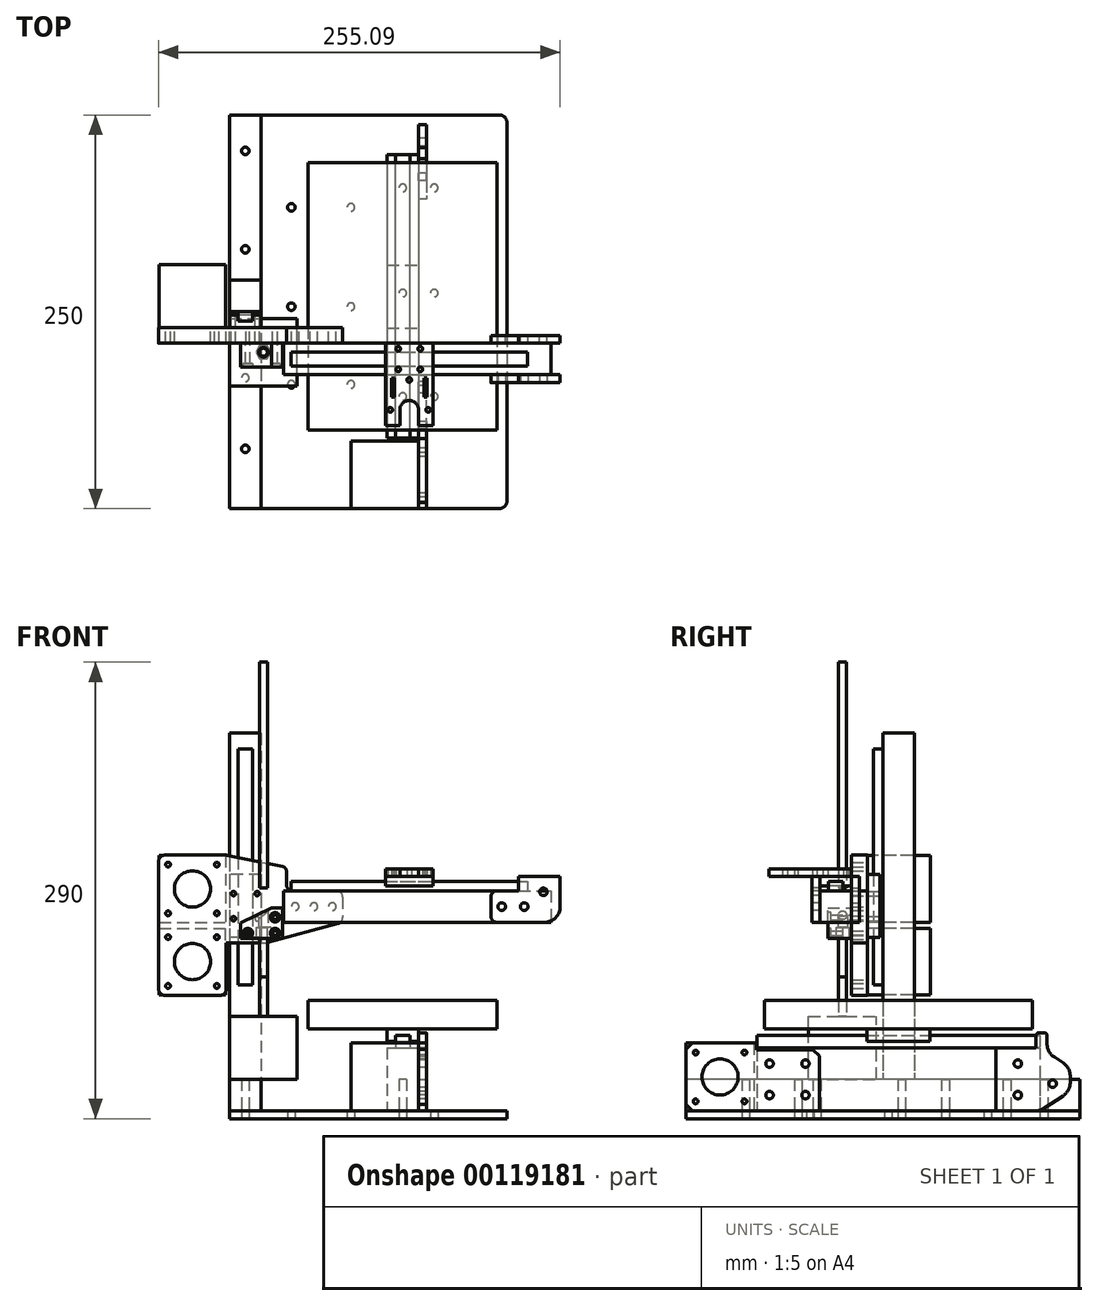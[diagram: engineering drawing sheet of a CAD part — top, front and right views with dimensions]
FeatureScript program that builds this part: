
annotation { "Feature Type Name" : "Feature", "Feature Type Description" : "" }
export const myFeature = defineFeature(function(context is Context, id is Id, definition is map)
    precondition{}
    {
        {
            var Q0;
            Q0=qCreatedBy(makeId("Top.planeOp"),FACE);
            var sketch = newSketch(context, id + "F0", { "sketchPlane" : qUnion([Q0])});
            skLineSegment(sketch, "E0.bottom", {"start": v(53.02, 129.2) * mm, "end": v(253.02, 129.2) * mm});
            skLineSegment(sketch, "E0.top", {"start": v(53.02, -120.8) * mm, "end": v(253.02, -120.8) * mm});
            skLineSegment(sketch, "E0.left", {"start": v(53.02, 129.2) * mm, "end": v(53.02, -120.8) * mm});
            skLineSegment(sketch, "E0.right", {"start": v(253.02, 129.2) * mm, "end": v(253.02, -120.8) * mm});
            skSolve(sketch);
        }
        {
            var Q0;
            Q0 = qSketchRegion(id + "F0", true);
            extrude(context, id + "F1", {"entities" : qUnion([Q0]), "depth" : 5 * mm});
        }
        {
            var Q0;
            Q0=makeQuery(id+"F1.opExtrude","CAP_FACE",FACE,{"disambiguationData":[OSD([sQuery(id+"F0.wireOp",EDGE,"E0.bottom"),sQuery(id+"F0.wireOp",EDGE,"E0.top"),sQuery(id+"F0.wireOp",EDGE,"E0.left"),sQuery(id+"F0.wireOp",EDGE,"E0.right")])],"isStart":false});
            var sketch = newSketch(context, id + "F2", { "sketchPlane" : qUnion([Q0])});
            skLineSegment(sketch, "E1.bottom", {"start": v(53.02, 129.2) * mm, "end": v(73.02, 129.2) * mm});
            skLineSegment(sketch, "E1.top", {"start": v(53.02, -120.8) * mm, "end": v(73.02, -120.8) * mm});
            skLineSegment(sketch, "E1.left", {"start": v(53.02, 129.2) * mm, "end": v(53.02, -120.8) * mm});
            skLineSegment(sketch, "E1.right", {"start": v(73.02, 129.2) * mm, "end": v(73.02, -120.8) * mm});
            skLineSegment(sketch, "E2.bottom", {"start": v(130.02, -120.8) * mm, "end": v(173.02, -120.8) * mm});
            skLineSegment(sketch, "E2.top", {"start": v(130.02, -77.8) * mm, "end": v(173.02, -77.8) * mm});
            skLineSegment(sketch, "E2.left", {"start": v(130.02, -120.8) * mm, "end": v(130.02, -77.8) * mm});
            skLineSegment(sketch, "E2.right", {"start": v(173.02, -120.8) * mm, "end": v(173.02, -77.8) * mm});
            skPoint(sketch, "E3.firstSnap0", {"position": v(153.02, 129.2) * mm});
            skLineSegment(sketch, "E3.bottom", {"start": v(153.02, 104) * mm, "end": v(173.02, 104) * mm});
            skLineSegment(sketch, "E3.top", {"start": v(153.02, -76) * mm, "end": v(173.02, -76) * mm});
            skLineSegment(sketch, "E3.left", {"start": v(153.02, 104) * mm, "end": v(153.02, -76) * mm});
            skLineSegment(sketch, "E3.right", {"start": v(173.02, 104) * mm, "end": v(173.02, -76) * mm});
            skSolve(sketch);
        }
        {
            var Q0;
            Q0=makeQuery(id+"F2.imprint","IMPRINT",FACE,{"disambiguationData":[TD([[makeQuery(id+"F2.imprint","IMPRINT",EDGE,{"derivedFrom":sQuery(id+"F2.wireOp",EDGE,"E1.bottom")}),-1.0]])]});
            var Q1;
            Q1=makeQuery(id+"F2.imprint","IMPRINT",FACE,{"disambiguationData":[TD([[makeQuery(id+"F2.imprint","IMPRINT",EDGE,{"derivedFrom":sQuery(id+"F2.wireOp",EDGE,"E3.bottom")}),-1.0]])]});
            extrude(context, id + "F3", {"entities" : qUnion([Q0, Q1]), "depth" : 40 * mm});
        }
        {
            var Q0;
            Q0=makeQuery(id+"F2.imprint","IMPRINT",FACE,{"disambiguationData":[TD([[makeQuery(id+"F2.imprint","IMPRINT",EDGE,{"derivedFrom":sQuery(id+"F2.wireOp",EDGE,"E2.bottom")}),1.0]])]});
            extrude(context, id + "F4", {"entities" : qUnion([Q0]), "depth" : 43 * mm});
        }
        {
            var Q0;
            Q0=makeQuery(id+"F3.opExtrude","CAP_FACE",FACE,{"disambiguationData":[OSD([sQuery(id+"F2.wireOp",EDGE,"E3.bottom"),sQuery(id+"F2.wireOp",EDGE,"E3.top"),sQuery(id+"F2.wireOp",EDGE,"E3.left"),sQuery(id+"F2.wireOp",EDGE,"E3.right")])],"isStart":false});
            var sketch = newSketch(context, id + "F5", { "sketchPlane" : qUnion([Q0])});
            skLineSegment(sketch, "E4.bottom", {"start": v(158.52, -76) * mm, "end": v(167.52, -76) * mm});
            skLineSegment(sketch, "E4.top", {"start": v(158.52, 104) * mm, "end": v(167.52, 104) * mm});
            skLineSegment(sketch, "E4.left", {"start": v(158.52, -76) * mm, "end": v(158.52, 104) * mm});
            skLineSegment(sketch, "E4.right", {"start": v(167.52, -76) * mm, "end": v(167.52, 104) * mm});
            skPoint(sketch, "E4.middle", {"position": v(163.02, 14) * mm});
            skPoint(sketch, "E4.middle.positionSnap0", {"position": v(163.02, -76) * mm});
            skPoint(sketch, "E4.middle.positionSnap1", {"position": v(153.02, 14) * mm});
            skPoint(sketch, "E4.centerSnap0", {"position": v(163.02, -76) * mm});
            skPoint(sketch, "E4.centerSnap1", {"position": v(153.02, 14) * mm});
            skSolve(sketch);
        }
        {
            var Q0;
            Q0 = qSketchRegion(id + "F5", true);
            extrude(context, id + "F6", {"entities" : qUnion([Q0]), "depth" : 8 * mm});
        }
        {
            var Q0;
            Q0=makeQuery(id+"F4.opExtrude","SWEPT_FACE",FACE,{"disambiguationData":[OSD([sQuery(id+"F2.wireOp",EDGE,"E2.right")])]});
            var sketch = newSketch(context, id + "F7", { "sketchPlane" : qUnion([Q0])});
            skCircle(sketch, "E5", {"center": v(-99.3, 26.5) * mm, "radius": 11.5 * mm});
            skPoint(sketch, "E5.centerSnap0", {"position": v(-120.8, 26.5) * mm});
            skPoint(sketch, "E5.centerSnap1", {"position": v(-99.3, 48) * mm});
            skLineSegment(sketch, "E6", {"start": v(-99.3, 26.5) * mm, "end": v(-77.8, 48) * mm, "construction": true});
            skLineSegment(sketch, "E7", {"start": v(-99.3, 48) * mm, "end": v(-99.3, 5) * mm, "construction": true});
            skLineSegment(sketch, "E8", {"start": v(-120.8, 26.5) * mm, "end": v(-77.8, 26.5) * mm, "construction": true});
            skCircle(sketch, "E9", {"center": v(-83.8, 42) * mm, "radius": 1.5 * mm});
            skCircle(sketch, "E10.MirrorC", {"center": v(-114.8, 42) * mm, "radius": 1.5 * mm});
            skCircle(sketch, "E11.MirrorC", {"center": v(-114.8, 11) * mm, "radius": 1.5 * mm});
            skCircle(sketch, "E12.MirrorC", {"center": v(-83.8, 11) * mm, "radius": 1.5 * mm});
            skLineSegment(sketch, "E13.bottom", {"start": v(-120.8, 5) * mm, "end": v(-76.27, 5) * mm});
            skLineSegment(sketch, "E13.top", {"start": v(-120.8, 48) * mm, "end": v(-76.27, 48) * mm});
            skLineSegment(sketch, "E13.left", {"start": v(-120.8, 5) * mm, "end": v(-120.8, 48) * mm});
            skLineSegment(sketch, "E13.right", {"start": v(-76.27, 43.73) * mm, "end": v(-76.27, 48) * mm});
            skLineSegment(sketch, "E14.bottom", {"start": v(-76.27, 43.73) * mm, "end": v(-36.27, 43.73) * mm});
            skLineSegment(sketch, "E14.top", {"start": v(-76.27, 5) * mm, "end": v(-36.27, 5) * mm});
            skLineSegment(sketch, "E14.right", {"start": v(-36.27, 43.73) * mm, "end": v(-36.27, 5) * mm});
            skLineSegment(sketch, "E15.0", {"start": v(104, 45) * mm, "end": v(104, 25) * mm});
            skLineSegment(sketch, "E16", {"start": v(104, 25) * mm, "end": v(88.12, 25) * mm, "construction": true});
            skPoint(sketch, "E17.orphan", {"position": v(104, 5) * mm});
            skLineSegment(sketch, "E18", {"start": v(104, 35) * mm, "end": v(-72.06, 35) * mm, "construction": true});
            skCircle(sketch, "E19", {"center": v(-67.87, 35) * mm, "radius": 2.4 * mm});
            skCircle(sketch, "E20", {"center": v(-45.03, 35) * mm, "radius": 2.4 * mm});
            skCircle(sketch, "E21.MirrorC", {"center": v(-67.87, 15) * mm, "radius": 2.4 * mm});
            skCircle(sketch, "E22.MirrorC", {"center": v(-45.03, 15) * mm, "radius": 2.4 * mm});
            skSolve(sketch);
        }
        {
            var Q0;
            Q0 = qSketchRegion(id + "F7", true);
            extrude(context, id + "F8", {"entities" : qUnion([Q0]), "depth" : 5 * mm});
        }
        {
            var Q0;
            Q0=makeQuery(id+"F8.opExtrude","SWEPT_EDGE",EDGE,{"disambiguationData":[OSD([sQuery(id+"F7.wireOp",EDGE,"E13.top"),sQuery(id+"F7.wireOp",EDGE,"E13.left")])]});
            var Q1;
            Q1=makeQuery(id+"F8.opExtrude","SWEPT_EDGE",EDGE,{"disambiguationData":[OSD([sQuery(id+"F7.wireOp",EDGE,"E13.bottom"),sQuery(id+"F7.wireOp",EDGE,"E13.left")])]});
            var Q2;
            Q2=makeQuery(id+"F8.opExtrude","SWEPT_EDGE",EDGE,{"disambiguationData":[OSD([sQuery(id+"F7.wireOp",EDGE,"E14.bottom"),sQuery(id+"F7.wireOp",EDGE,"E14.right")])]});
            chamfer(context, id + "F9", {"entities" : qUnion([Q0, Q1, Q2]), "width" : 4 * mm, "tangentPropagation" : true});
        }
        {
            var Q0;
            Q0=makeQuery(id+"F3.opExtrude","SWEPT_FACE",FACE,{"disambiguationData":[OSD([sQuery(id+"F2.wireOp",EDGE,"E3.right")])]});
            var sketch = newSketch(context, id + "F10", { "sketchPlane" : qUnion([Q0])});
            skLineSegment(sketch, "E23.0", {"start": v(104, 45) * mm, "end": v(104, 25) * mm, "construction": true});
            skLineSegment(sketch, "E24", {"start": v(104, 25) * mm, "end": v(84.3, 25) * mm, "construction": true});
            skPoint(sketch, "E25.orphan", {"position": v(104, 5) * mm});
            skCircle(sketch, "E26", {"center": v(89.85, 35) * mm, "radius": 2.4 * mm});
            skPoint(sketch, "E26.centerSnap0", {"position": v(104, 35) * mm});
            skCircle(sketch, "E27.MirrorC", {"center": v(89.85, 15) * mm, "radius": 2.4 * mm});
            skLineSegment(sketch, "E28.bottom", {"start": v(75.87, 45) * mm, "end": v(101.38, 45) * mm});
            skLineSegment(sketch, "E28.top", {"start": v(75.87, 5) * mm, "end": v(104, 5) * mm});
            skLineSegment(sketch, "E28.left", {"start": v(75.87, 45) * mm, "end": v(75.87, 5) * mm});
            skLineSegment(sketch, "E28.right", {"start": v(123.14, 32.4) * mm, "end": v(123.14, 17.6) * mm});
            skLineSegment(sketch, "E29", {"start": v(-99.33, 32.4) * mm, "end": v(131.84, 32.4) * mm, "construction": true});
            skCircle(sketch, "E30", {"center": v(111.96, 22.22) * mm, "radius": 10.5 * mm, "construction": true});
            skCircle(sketch, "E31", {"center": v(111.96, 22.22) * mm, "radius": 2.4 * mm});
            skLineSegment(sketch, "E32", {"start": v(108.43, 42.08) * mm, "end": v(123.14, 32.4) * mm});
            skLineSegment(sketch, "E33.MirrorCS", {"start": v(104, 5) * mm, "end": v(123.14, 17.6) * mm});
            skPoint(sketch, "E34.orphan", {"position": v(123.14, 5) * mm});
            skLineSegment(sketch, "E35.top", {"start": v(101.38, 54.64) * mm, "end": v(108.43, 54.64) * mm});
            skLineSegment(sketch, "E35.left", {"start": v(101.38, 45) * mm, "end": v(101.38, 54.64) * mm});
            skLineSegment(sketch, "E35.right", {"start": v(108.43, 42.08) * mm, "end": v(108.43, 54.64) * mm});
            skSolve(sketch);
        }
        {
            var Q0;
            Q0 = qSketchRegion(id + "F10", true);
            extrude(context, id + "F11", {"entities" : qUnion([Q0]), "depth" : 5 * mm});
        }
        {
            var Q0;
            Q0=makeQuery(id+"F11.opExtrude","SWEPT_EDGE",EDGE,{"disambiguationData":[OSD([sQuery(id+"F10.wireOp",EDGE,"E32"),sQuery(id+"F10.wireOp",EDGE,"E35.right")])]});
            var Q1;
            Q1=makeQuery(id+"F11.opExtrude","SWEPT_EDGE",EDGE,{"disambiguationData":[OSD([sQuery(id+"F10.wireOp",EDGE,"E28.right"),sQuery(id+"F10.wireOp",EDGE,"E32")])]});
            var Q2;
            Q2=makeQuery(id+"F11.opExtrude","SWEPT_EDGE",EDGE,{"disambiguationData":[OSD([sQuery(id+"F10.wireOp",EDGE,"E28.right"),sQuery(id+"F10.wireOp",EDGE,"E33.MirrorCS")])]});
            var Q3;
            Q3=makeQuery(id+"F11.opExtrude","SWEPT_EDGE",EDGE,{"disambiguationData":[OSD([sQuery(id+"F2.wireOp",EDGE,"E3.bottom"),sQuery(id+"F2.wireOp",EDGE,"E3.right"),sQuery(id+"F10.wireOp",EDGE,"E28.top"),sQuery(id+"F10.wireOp",EDGE,"E33.MirrorCS")])]});
            fillet(context, id + "F12", {"entities" : qUnion([Q0, Q1, Q2, Q3]), "radius" : 10 * mm, "tangentPropagation" : true, "allowEdgeOverflow" : false});
        }
        {
            var Q0;
            Q0=makeQuery(id+"F11.opExtrude","SWEPT_EDGE",EDGE,{"disambiguationData":[OSD([sQuery(id+"F10.wireOp",EDGE,"E35.top"),sQuery(id+"F10.wireOp",EDGE,"E35.right")])]});
            var Q1;
            Q1=makeQuery(id+"F11.opExtrude","SWEPT_EDGE",EDGE,{"disambiguationData":[OSD([sQuery(id+"F10.wireOp",EDGE,"E35.top"),sQuery(id+"F10.wireOp",EDGE,"E35.left")])]});
            fillet(context, id + "F13", {"entities" : qUnion([Q0, Q1]), "radius" : 2 * mm, "tangentPropagation" : true, "allowEdgeOverflow" : false});
        }
        {
            var Q0;
            Q0=makeQuery(id+"F6.opExtrude","CAP_FACE",FACE,{"disambiguationData":[OSD([sQuery(id+"F5.wireOp",EDGE,"E4.bottom"),sQuery(id+"F5.wireOp",EDGE,"E4.top"),sQuery(id+"F5.wireOp",EDGE,"E4.left"),sQuery(id+"F5.wireOp",EDGE,"E4.right")])],"isStart":false});
            var sketch = newSketch(context, id + "F14", { "sketchPlane" : qUnion([Q0])});
            skLineSegment(sketch, "E36.0", {"start": v(153.02, 104) * mm, "end": v(153.02, -76) * mm, "construction": true});
            skLineSegment(sketch, "E37.bottom", {"start": v(153.02, 34) * mm, "end": v(173.02, 34) * mm});
            skLineSegment(sketch, "E37.top", {"start": v(153.02, -6) * mm, "end": v(173.02, -6) * mm});
            skLineSegment(sketch, "E37.left", {"start": v(153.02, 34) * mm, "end": v(153.02, -6) * mm});
            skLineSegment(sketch, "E37.right", {"start": v(173.02, 34) * mm, "end": v(173.02, -6) * mm});
            skPoint(sketch, "E37.middle", {"position": v(163.02, 14) * mm});
            skPoint(sketch, "E37.middle.positionSnap0", {"position": v(163.02, -76) * mm});
            skPoint(sketch, "E37.middle.positionSnap1", {"position": v(167.52, 14) * mm});
            skPoint(sketch, "E37.centerSnap0", {"position": v(163.02, -76) * mm});
            skPoint(sketch, "E37.centerSnap1", {"position": v(167.52, 14) * mm});
            skSolve(sketch);
        }
        {
            var Q0;
            Q0 = qSketchRegion(id + "F14", true);
            extrude(context, id + "F15", {"entities" : qUnion([Q0]), "endBound" : BoundingType.SYMMETRIC, "depth" : 8 * mm});
        }
        {
            var Q0;
            Q0=makeQuery(id+"F0.imprint","IMPRINT",FACE,{"disambiguationData":[TD([[makeQuery(id+"F0.imprint","IMPRINT",EDGE,{"derivedFrom":sQuery(id+"F0.wireOp",EDGE,"E0.bottom")}),-1.0]])]});
            var sketch = newSketch(context, id + "F16", { "sketchPlane" : qUnion([Q0])});
            skLineSegment(sketch, "E38.0", {"start": v(153.02, 104) * mm, "end": v(173.02, 104) * mm, "construction": true});
            skLineSegment(sketch, "E39.0", {"start": v(73.02, 129.2) * mm, "end": v(73.02, -120.8) * mm, "construction": true});
            skLineSegment(sketch, "E40", {"start": v(73.02, -120.8) * mm, "end": v(53.02, -120.8) * mm, "construction": true});
            skCircle(sketch, "E41", {"center": v(63.02, -82.87) * mm, "radius": 2.4 * mm});
            skPoint(sketch, "E41.centerSnap0", {"position": v(63.02, -120.8) * mm});
            skCircle(sketch, "E42", {"center": v(63.02, -37.77) * mm, "radius": 2.4 * mm});
            skCircle(sketch, "E43", {"center": v(63.02, 43.87) * mm, "radius": 2.4 * mm});
            skCircle(sketch, "E44", {"center": v(63.02, 106.4) * mm, "radius": 2.4 * mm});
            skCircle(sketch, "E45", {"center": v(163.02, 82.91) * mm, "radius": 2.4 * mm});
            skPoint(sketch, "E45.centerSnap0", {"position": v(163.02, 104) * mm});
            skCircle(sketch, "E46", {"center": v(163.02, 16.05) * mm, "radius": 2.4 * mm});
            skCircle(sketch, "E47", {"center": v(163.02, -49.65) * mm, "radius": 2.4 * mm});
            skCircle(sketch, "E48", {"center": v(92.26, 70.57) * mm, "radius": 2.4 * mm});
            skCircle(sketch, "E49", {"center": v(130.12, 70.57) * mm, "radius": 2.4 * mm});
            skCircle(sketch, "E50", {"center": v(92.26, 7.46) * mm, "radius": 2.4 * mm});
            skCircle(sketch, "E51", {"center": v(130.12, 7.46) * mm, "radius": 2.4 * mm});
            skCircle(sketch, "E52", {"center": v(92.26, -41.93) * mm, "radius": 2.4 * mm});
            skCircle(sketch, "E53", {"center": v(130.12, -41.93) * mm, "radius": 2.4 * mm});
            skLineSegment(sketch, "E54.bottom", {"start": v(223.02, -73.95) * mm, "end": v(103.02, -73.95) * mm, "construction": true});
            skLineSegment(sketch, "E54.top", {"start": v(223.02, 106.05) * mm, "end": v(103.02, 106.05) * mm, "construction": true});
            skLineSegment(sketch, "E54.left", {"start": v(223.02, -73.95) * mm, "end": v(223.02, 106.05) * mm, "construction": true});
            skLineSegment(sketch, "E54.right", {"start": v(103.02, -73.95) * mm, "end": v(103.02, 106.05) * mm, "construction": true});
            skLineSegment(sketch, "E55.bottom", {"start": v(229.27, -124.8) * mm, "end": v(278.84, -124.8) * mm});
            skLineSegment(sketch, "E55.top", {"start": v(229.27, 139.17) * mm, "end": v(278.84, 139.17) * mm});
            skLineSegment(sketch, "E55.left", {"start": v(229.27, -124.8) * mm, "end": v(229.27, 139.17) * mm});
            skLineSegment(sketch, "E55.right", {"start": v(278.84, -124.8) * mm, "end": v(278.84, 139.17) * mm});
            skCircle(sketch, "E56.MirrorC", {"center": v(183.02, -49.65) * mm, "radius": 2.4 * mm});
            skCircle(sketch, "E57.MirrorC", {"center": v(183.02, 16.05) * mm, "radius": 2.4 * mm});
            skCircle(sketch, "E58.MirrorC", {"center": v(183.02, 82.91) * mm, "radius": 2.4 * mm});
            skSolve(sketch);
        }
        {
            var Q0;
            Q0 = qSketchRegion(id + "F16", true);
            extrude(context, id + "F17", {"entities" : qUnion([Q0]), "operationType" : NewBodyOperationType.REMOVE, "depth" : 25 * mm});
        }
        {
            var Q0;
            Q0=makeQuery(id+"F17.boolean.opBoolean","INTERSECT",EDGE,{"derivedFrom":[makeQuery(id+"F1.opExtrude","SWEPT_FACE",FACE,{"disambiguationData":[OSD([sQuery(id+"F0.wireOp",EDGE,"E0.top")])]}),makeQuery(id+"F17.opExtrude","SWEPT_FACE",FACE,{"disambiguationData":[OSD([sQuery(id+"F16.wireOp",EDGE,"E55.left")])]})]});
            var Q1;
            Q1=makeQuery(id+"F17.boolean.opBoolean","INTERSECT",EDGE,{"derivedFrom":[makeQuery(id+"F1.opExtrude","SWEPT_FACE",FACE,{"disambiguationData":[OSD([sQuery(id+"F0.wireOp",EDGE,"E0.bottom")])]}),makeQuery(id+"F17.opExtrude","SWEPT_FACE",FACE,{"disambiguationData":[OSD([sQuery(id+"F16.wireOp",EDGE,"E55.left")])]})]});
            fillet(context, id + "F18", {"entities" : qUnion([Q0, Q1]), "radius" : 5 * mm, "tangentPropagation" : true, "allowEdgeOverflow" : false});
        }
        {
            var Q0;
            Q0=makeQuery(id+"F3.opExtrude","CAP_FACE",FACE,{"disambiguationData":[OSD([sQuery(id+"F2.wireOp",EDGE,"E1.bottom"),sQuery(id+"F2.wireOp",EDGE,"E1.top"),sQuery(id+"F2.wireOp",EDGE,"E1.left"),sQuery(id+"F2.wireOp",EDGE,"E1.right")])],"isStart":false});
            extrude(context, id + "F19", {"entities" : qUnion([Q0]), "operationType" : NewBodyOperationType.REMOVE, "oppositeDirection" : true, "depth" : 20 * mm});
        }
        {
            var Q0;
            Q0=makeQuery(id+"F19.boolean.opBoolean","COPY",FACE,{"derivedFrom":makeQuery(id+"F19.opExtrude","CAP_FACE",FACE,{"disambiguationData":[OSD([sQuery(id+"F2.wireOp",EDGE,"E1.bottom"),sQuery(id+"F2.wireOp",EDGE,"E1.top"),sQuery(id+"F2.wireOp",EDGE,"E1.left"),sQuery(id+"F2.wireOp",EDGE,"E1.right")])],"isStart":false})});
            var sketch = newSketch(context, id + "F20", { "sketchPlane" : qUnion([Q0])});
            skLineSegment(sketch, "E59.bottom", {"start": v(73.02, 24.2) * mm, "end": v(53.02, 24.2) * mm});
            skLineSegment(sketch, "E59.top", {"start": v(73.02, 4.2) * mm, "end": v(53.02, 4.2) * mm});
            skLineSegment(sketch, "E59.left", {"start": v(73.02, 24.2) * mm, "end": v(73.02, 4.2) * mm});
            skLineSegment(sketch, "E59.right", {"start": v(53.02, 24.2) * mm, "end": v(53.02, 4.2) * mm});
            skSolve(sketch);
        }
        {
            var Q0;
            Q0 = qSketchRegion(id + "F20", true);
            extrude(context, id + "F21", {"entities" : qUnion([Q0]), "depth" : 220 * mm});
        }
        {
            var Q0;
            Q0=makeQuery(id+"F21.opExtrude","SWEPT_FACE",FACE,{"disambiguationData":[OSD([sQuery(id+"F20.wireOp",EDGE,"E59.top")])]});
            var sketch = newSketch(context, id + "F22", { "sketchPlane" : qUnion([Q0])});
            skLineSegment(sketch, "E60.bottom", {"start": v(67.52, 234.96) * mm, "end": v(58.52, 234.96) * mm});
            skLineSegment(sketch, "E60.top", {"start": v(67.52, 35.04) * mm, "end": v(58.52, 35.04) * mm});
            skLineSegment(sketch, "E60.left", {"start": v(67.52, 234.96) * mm, "end": v(67.52, 35.04) * mm});
            skLineSegment(sketch, "E60.right", {"start": v(58.52, 234.96) * mm, "end": v(58.52, 35.04) * mm});
            skPoint(sketch, "E60.middle", {"position": v(63.02, 135) * mm});
            skPoint(sketch, "E60.middle.positionSnap0", {"position": v(63.02, 245) * mm});
            skPoint(sketch, "E60.middle.positionSnap1", {"position": v(53.02, 135) * mm});
            skPoint(sketch, "E60.centerSnap0", {"position": v(63.02, 245) * mm});
            skPoint(sketch, "E60.centerSnap1", {"position": v(53.02, 135) * mm});
            skSolve(sketch);
        }
        {
            var Q0;
            Q0 = qSketchRegion(id + "F22", true);
            extrude(context, id + "F23", {"entities" : qUnion([Q0]), "depth" : 6 * mm});
        }
        {
            var Q0;
            Q0=makeQuery(id+"F23.opExtrude","CAP_FACE",FACE,{"disambiguationData":[OSD([sQuery(id+"F22.wireOp",EDGE,"E60.bottom"),sQuery(id+"F22.wireOp",EDGE,"E60.top"),sQuery(id+"F22.wireOp",EDGE,"E60.left"),sQuery(id+"F22.wireOp",EDGE,"E60.right")])],"isStart":false});
            var sketch = newSketch(context, id + "F24", { "sketchPlane" : qUnion([Q0])});
            skLineSegment(sketch, "E61.bottom", {"start": v(73.02, 155) * mm, "end": v(53.02, 155) * mm});
            skLineSegment(sketch, "E61.top", {"start": v(73.02, 115) * mm, "end": v(53.02, 115) * mm});
            skLineSegment(sketch, "E61.left", {"start": v(73.02, 155) * mm, "end": v(73.02, 115) * mm});
            skLineSegment(sketch, "E61.right", {"start": v(53.02, 155) * mm, "end": v(53.02, 115) * mm});
            skPoint(sketch, "E61.middle", {"position": v(63.02, 135) * mm});
            skPoint(sketch, "E61.middle.positionSnap0", {"position": v(67.52, 135) * mm});
            skPoint(sketch, "E61.middle.positionSnap1", {"position": v(63.02, 234.96) * mm});
            skPoint(sketch, "E61.centerSnap0", {"position": v(67.52, 135) * mm});
            skPoint(sketch, "E61.centerSnap1", {"position": v(63.02, 234.96) * mm});
            skLineSegment(sketch, "E62.bottom", {"start": v(70.52, 143) * mm, "end": v(55.52, 143) * mm, "construction": true});
            skLineSegment(sketch, "E62.top", {"start": v(70.52, 127) * mm, "end": v(55.52, 127) * mm, "construction": true});
            skLineSegment(sketch, "E62.left", {"start": v(70.52, 143) * mm, "end": v(70.52, 127) * mm, "construction": true});
            skLineSegment(sketch, "E62.right", {"start": v(55.52, 143) * mm, "end": v(55.52, 127) * mm, "construction": true});
            skCircle(sketch, "E63", {"center": v(55.52, 143) * mm, "radius": 1.4 * mm});
            skCircle(sketch, "E64", {"center": v(70.52, 143) * mm, "radius": 1.4 * mm});
            skCircle(sketch, "E65", {"center": v(55.52, 127) * mm, "radius": 1.4 * mm});
            skCircle(sketch, "E66", {"center": v(70.52, 127) * mm, "radius": 1.4 * mm});
            skSolve(sketch);
        }
        {
            var Q0;
            Q0 = qSketchRegion(id + "F24", true);
            extrude(context, id + "F25", {"entities" : qUnion([Q0]), "endBound" : BoundingType.SYMMETRIC, "depth" : 8 * mm});
        }
        {
            var Q0;
            Q0=makeQuery(id+"F23.opExtrude","SWEPT_FACE",FACE,{"disambiguationData":[OSD([sQuery(id+"F22.wireOp",EDGE,"E60.top")])]});
            extrude(context, id + "F26", {"entities" : qUnion([Q0]), "operationType" : NewBodyOperationType.REMOVE, "oppositeDirection" : true, "depth" : 50 * mm});
        }
        {
            var Q0;
            Q0=makeQuery(id+"F25.opExtrude","CAP_FACE",FACE,{"disambiguationData":[OSD([sQuery(id+"F24.wireOp",EDGE,"E61.bottom"),sQuery(id+"F24.wireOp",EDGE,"E61.top"),sQuery(id+"F24.wireOp",EDGE,"E61.left"),sQuery(id+"F24.wireOp",EDGE,"E61.right"),sQuery(id+"F24.wireOp",EDGE,"E63"),sQuery(id+"F24.wireOp",EDGE,"E64"),sQuery(id+"F24.wireOp",EDGE,"E65"),sQuery(id+"F24.wireOp",EDGE,"E66")])],"isStart":false});
            var sketch = newSketch(context, id + "F27", { "sketchPlane" : qUnion([Q0])});
            skLineSegment(sketch, "E67.bottom", {"start": v(89.11, 144.7) * mm, "end": v(259.11, 144.7) * mm, "construction": true});
            skLineSegment(sketch, "E67.top", {"start": v(89.11, 124.7) * mm, "end": v(259.11, 124.7) * mm, "construction": true});
            skLineSegment(sketch, "E67.left", {"start": v(89.11, 144.7) * mm, "end": v(89.11, 124.7) * mm, "construction": true});
            skLineSegment(sketch, "E67.right", {"start": v(259.11, 144.7) * mm, "end": v(259.11, 124.7) * mm, "construction": true});
            skCircle(sketch, "E68.0", {"center": v(55.52, 143) * mm, "radius": 1.4 * mm});
            skCircle(sketch, "E69.0", {"center": v(70.52, 143) * mm, "radius": 1.4 * mm});
            skCircle(sketch, "E70.0", {"center": v(70.52, 127) * mm, "radius": 1.4 * mm});
            skCircle(sketch, "E71.0", {"center": v(55.52, 127) * mm, "radius": 1.4 * mm});
            skLineSegment(sketch, "E72.bottom", {"start": v(156.82, 144.7) * mm, "end": v(165.82, 144.7) * mm, "construction": true});
            skLineSegment(sketch, "E72.top", {"start": v(156.82, 153.7) * mm, "end": v(165.82, 153.7) * mm, "construction": true});
            skLineSegment(sketch, "E72.left", {"start": v(156.82, 144.7) * mm, "end": v(156.82, 153.7) * mm, "construction": true});
            skLineSegment(sketch, "E72.right", {"start": v(165.82, 144.7) * mm, "end": v(165.82, 153.7) * mm, "construction": true});
            skLineSegment(sketch, "E73", {"start": v(156.82, 153.7) * mm, "end": v(17.3, 153.7) * mm, "construction": true});
            skLineSegment(sketch, "E74.bottom", {"start": v(50.93, 124.4) * mm, "end": v(7.93, 124.4) * mm, "construction": true});
            skLineSegment(sketch, "E74.top", {"start": v(50.93, 167.4) * mm, "end": v(7.93, 167.4) * mm, "construction": true});
            skLineSegment(sketch, "E74.left", {"start": v(50.93, 124.4) * mm, "end": v(50.93, 167.4) * mm, "construction": true});
            skLineSegment(sketch, "E74.right", {"start": v(7.93, 124.4) * mm, "end": v(7.93, 167.4) * mm, "construction": true});
            skPoint(sketch, "E74.middle", {"position": v(29.43, 145.9) * mm});
            skCircle(sketch, "E75", {"center": v(29.43, 145.9) * mm, "radius": 6 * mm, "construction": true});
            skLineSegment(sketch, "E76", {"start": v(268.66, 134.7) * mm, "end": v(73.02, 134.7) * mm, "construction": true});
            skPoint(sketch, "E76.startSnap0", {"position": v(89.11, 134.7) * mm});
            skLineSegment(sketch, "E77", {"start": v(50.93, 122.85) * mm, "end": v(4.58, 122.85) * mm, "construction": true});
            skLineSegment(sketch, "E78", {"start": v(29.43, 145.9) * mm, "end": v(50.93, 167.4) * mm, "construction": true});
            skLineSegment(sketch, "E79", {"start": v(29.43, 167.4) * mm, "end": v(29.43, 124.4) * mm, "construction": true});
            skLineSegment(sketch, "E80", {"start": v(7.93, 145.9) * mm, "end": v(50.93, 145.9) * mm, "construction": true});
            skCircle(sketch, "E81", {"center": v(44.93, 161.4) * mm, "radius": 1.5 * mm});
            skCircle(sketch, "E82.MirrorC", {"center": v(13.93, 161.4) * mm, "radius": 1.5 * mm});
            skCircle(sketch, "E83.MirrorC", {"center": v(44.93, 130.4) * mm, "radius": 1.5 * mm});
            skCircle(sketch, "E84.MirrorC", {"center": v(13.93, 130.4) * mm, "radius": 1.5 * mm});
            skCircle(sketch, "E85", {"center": v(29.43, 145.9) * mm, "radius": 11.5 * mm});
            skCircle(sketch, "E86.MirrorC", {"center": v(13.93, 84.3) * mm, "radius": 1.5 * mm});
            skLineSegment(sketch, "E87.MirrorCS", {"start": v(50.93, 121.3) * mm, "end": v(7.93, 121.3) * mm, "construction": true});
            skLineSegment(sketch, "E88.MirrorCS", {"start": v(50.93, 78.3) * mm, "end": v(7.93, 78.3) * mm, "construction": true});
            skLineSegment(sketch, "E89.MirrorCS", {"start": v(50.93, 121.3) * mm, "end": v(50.93, 78.3) * mm, "construction": true});
            skLineSegment(sketch, "E90.MirrorCS", {"start": v(29.43, 78.3) * mm, "end": v(29.43, 121.3) * mm, "construction": true});
            skCircle(sketch, "E91.MirrorC", {"center": v(44.93, 115.3) * mm, "radius": 1.5 * mm});
            skCircle(sketch, "E92.MirrorC", {"center": v(29.43, 99.8) * mm, "radius": 11.5 * mm});
            skLineSegment(sketch, "E93.MirrorCS", {"start": v(7.93, 121.3) * mm, "end": v(7.93, 78.3) * mm, "construction": true});
            skLineSegment(sketch, "E94.MirrorCS", {"start": v(29.43, 99.8) * mm, "end": v(50.93, 78.3) * mm, "construction": true});
            skLineSegment(sketch, "E95.MirrorCS", {"start": v(7.93, 99.8) * mm, "end": v(50.93, 99.8) * mm, "construction": true});
            skCircle(sketch, "E96.MirrorC", {"center": v(44.93, 84.3) * mm, "radius": 1.5 * mm});
            skCircle(sketch, "E97.MirrorC", {"center": v(13.93, 115.3) * mm, "radius": 1.5 * mm});
            skCircle(sketch, "E98.MirrorC", {"center": v(29.43, 99.8) * mm, "radius": 6 * mm, "construction": true});
            skLineSegment(sketch, "E99.bottom", {"start": v(7.93, 167.4) * mm, "end": v(50.93, 167.4) * mm});
            skLineSegment(sketch, "E99.top", {"start": v(7.93, 78.3) * mm, "end": v(50.93, 78.3) * mm});
            skLineSegment(sketch, "E99.left", {"start": v(7.93, 167.4) * mm, "end": v(7.93, 78.3) * mm});
            skLineSegment(sketch, "E99.right", {"start": v(124.85, 144.7) * mm, "end": v(124.85, 124.7) * mm});
            skCircle(sketch, "E100", {"center": v(94.67, 134.7) * mm, "radius": 2.4 * mm});
            skCircle(sketch, "E101", {"center": v(106.62, 134.7) * mm, "radius": 2.4 * mm});
            skCircle(sketch, "E102", {"center": v(118.31, 134.7) * mm, "radius": 2.4 * mm});
            skLineSegment(sketch, "E103", {"start": v(50.93, 167.4) * mm, "end": v(73.7, 162.82) * mm});
            skLineSegment(sketch, "E104", {"start": v(89.11, 144.7) * mm, "end": v(124.85, 144.7) * mm});
            skLineSegment(sketch, "E105", {"start": v(50.93, 78.3) * mm, "end": v(50.93, 111.72) * mm});
            skLineSegment(sketch, "E106", {"start": v(50.93, 111.72) * mm, "end": v(76.34, 111.72) * mm});
            skLineSegment(sketch, "E107", {"start": v(76.34, 111.72) * mm, "end": v(124.85, 124.7) * mm});
            skPoint(sketch, "E108.orphan", {"position": v(124.85, 78.3) * mm});
            skLineSegment(sketch, "E109.bottom", {"start": v(241.65, 124.7) * mm, "end": v(275.72, 124.7) * mm});
            skLineSegment(sketch, "E109.top", {"start": v(259.11, 153.9) * mm, "end": v(285.72, 153.9) * mm});
            skLineSegment(sketch, "E109.left", {"start": v(241.65, 124.7) * mm, "end": v(241.65, 144.7) * mm});
            skLineSegment(sketch, "E109.right", {"start": v(285.72, 134.7) * mm, "end": v(285.72, 153.9) * mm});
            skCircle(sketch, "E110", {"center": v(248.57, 134.7) * mm, "radius": 2.4 * mm});
            skCircle(sketch, "E111", {"center": v(262.85, 134.7) * mm, "radius": 2.4 * mm});
            skLineSegment(sketch, "E112", {"start": v(241.65, 144.7) * mm, "end": v(259.11, 144.7) * mm});
            skLineSegment(sketch, "E113", {"start": v(259.11, 144.7) * mm, "end": v(259.11, 159.61) * mm});
            skLineSegment(sketch, "E114", {"start": v(165.82, 153.7) * mm, "end": v(241.65, 153.82) * mm, "construction": true});
            skCircle(sketch, "E115", {"center": v(275.06, 144.07) * mm, "radius": 8 * mm, "construction": true});
            skCircle(sketch, "E116", {"center": v(275.06, 144.07) * mm, "radius": 2.4 * mm});
            skPoint(sketch, "E117.visualSharp", {"position": v(285.72, 124.7) * mm});
            skArc(sketch, "E117.filletArc", {"start": v(275.72, 124.7) * mm, "mid": v(282.8, 127.64) * mm, "end": v(285.72, 134.7) * mm});
            skLineSegment(sketch, "E118.trimOffspring", {"start": v(285.72, 153.88) * mm, "end": v(291.96, 153.9) * mm, "construction": true});
            skLineSegment(sketch, "E119.trimOffspring", {"start": v(241.65, 153.82) * mm, "end": v(241.65, 153.9) * mm});
            skLineSegment(sketch, "E120.top", {"start": v(285.72, 153.9) * mm, "end": v(259.11, 153.9) * mm});
            skLineSegment(sketch, "E120.left", {"start": v(285.72, 150.28) * mm, "end": v(285.72, 153.9) * mm});
            skLineSegment(sketch, "E120.right", {"start": v(259.11, 153.9) * mm, "end": v(259.11, 159.61) * mm});
            skPoint(sketch, "E121", {"position": v(74.62, 113.7) * mm});
            skCircle(sketch, "E122", {"center": v(64.61, 117.89) * mm, "radius": 1.25 * mm});
            skCircle(sketch, "E123", {"center": v(81.96, 117.89) * mm, "radius": 1.5 * mm});
            skCircle(sketch, "E124", {"center": v(81.96, 127.9) * mm, "radius": 1.5 * mm});
            skLineSegment(sketch, "E125", {"start": v(73.7, 162.82) * mm, "end": v(89.11, 159.7) * mm});
            skLineSegment(sketch, "E126", {"start": v(89.11, 159.7) * mm, "end": v(89.11, 144.7) * mm});
            skPoint(sketch, "E127.orphan", {"position": v(74.27, 144.7) * mm});
            skSolve(sketch);
        }
        {
            var Q0;
            Q0 = qSketchRegion(id + "F27", true);
            extrude(context, id + "F28", {"entities" : qUnion([Q0]), "depth" : 10 * mm});
        }
        {
            var Q0;
            Q0=makeQuery(id+"F28.opExtrude","SWEPT_EDGE",EDGE,{"disambiguationData":[OSD([sQuery(id+"F27.wireOp",EDGE,"TEMbkpEK-8kXP-iDgy-SPFr-wUDxhQlcmG9e"),sQuery(id+"F27.wireOp",EDGE,"E104")])]});
            var Q1;
            Q1=makeQuery(id+"F28.opExtrude","SWEPT_EDGE",EDGE,{"disambiguationData":[OSD([sQuery(id+"F27.wireOp",EDGE,"E103"),sQuery(id+"F27.wireOp",EDGE,"TEMbkpEK-8kXP-iDgy-SPFr-wUDxhQlcmG9e")])]});
            var Q2;
            Q2=makeQuery(id+"F28.opExtrude","SWEPT_EDGE",EDGE,{"disambiguationData":[OSD([sQuery(id+"F27.wireOp",EDGE,"E99.bottom"),sQuery(id+"F27.wireOp",EDGE,"E103")])]});
            var Q3;
            Q3=makeQuery(id+"F28.opExtrude","SWEPT_EDGE",EDGE,{"disambiguationData":[OSD([sQuery(id+"F27.wireOp",EDGE,"E99.right"),sQuery(id+"F27.wireOp",EDGE,"E104")])]});
            var Q4;
            Q4=makeQuery(id+"F28.opExtrude","SWEPT_EDGE",EDGE,{"disambiguationData":[OSD([sQuery(id+"F27.wireOp",EDGE,"E99.right"),sQuery(id+"F27.wireOp",EDGE,"E107")])]});
            var Q5;
            Q5=makeQuery(id+"F28.opExtrude","SWEPT_EDGE",EDGE,{"disambiguationData":[OSD([sQuery(id+"F27.wireOp",EDGE,"E99.bottom"),sQuery(id+"F27.wireOp",EDGE,"E99.left")])]});
            var Q6;
            Q6=makeQuery(id+"F28.opExtrude","SWEPT_EDGE",EDGE,{"disambiguationData":[OSD([sQuery(id+"F27.wireOp",EDGE,"E99.top"),sQuery(id+"F27.wireOp",EDGE,"E99.left")])]});
            var Q7;
            Q7=makeQuery(id+"F28.opExtrude","SWEPT_EDGE",EDGE,{"disambiguationData":[OSD([sQuery(id+"F27.wireOp",EDGE,"E99.top"),sQuery(id+"F27.wireOp",EDGE,"E105")])]});
            var Q8;
            Q8=makeQuery(id+"F28.opExtrude","SWEPT_EDGE",EDGE,{"disambiguationData":[OSD([sQuery(id+"F27.wireOp",EDGE,"E106"),sQuery(id+"F27.wireOp",EDGE,"E107")])]});
            var Q9;
            Q9=makeQuery(id+"F28.opExtrude","SWEPT_EDGE",EDGE,{"disambiguationData":[OSD([sQuery(id+"F27.wireOp",EDGE,"E120.top"),sQuery(id+"F27.wireOp",EDGE,"E120.left")])]});
            var Q10;
            Q10=makeQuery(id+"F28.opExtrude","SWEPT_EDGE",EDGE,{"disambiguationData":[OSD([sQuery(id+"F27.wireOp",EDGE,"E120.top"),sQuery(id+"F27.wireOp",EDGE,"E120.right")])]});
            var Q11;
            Q11=makeQuery(id+"F28.opExtrude","SWEPT_EDGE",EDGE,{"disambiguationData":[OSD([sQuery(id+"F27.wireOp",EDGE,"E109.left"),sQuery(id+"F27.wireOp",EDGE,"E112")])]});
            var Q12;
            Q12=makeQuery(id+"F28.opExtrude","SWEPT_EDGE",EDGE,{"disambiguationData":[OSD([sQuery(id+"F27.wireOp",EDGE,"E109.bottom"),sQuery(id+"F27.wireOp",EDGE,"E109.left")])]});
            fillet(context, id + "F29", {"entities" : qUnion([Q0, Q1, Q2, Q3, Q4, Q5, Q6, Q7, Q8, Q9, Q10, Q11, Q12]), "radius" : 4 * mm, "tangentPropagation" : true, "allowEdgeOverflow" : false});
        }
        {
            var Q0;
            Q0=qCreatedBy(makeId("Front.planeOp"),FACE);
            var sketch = newSketch(context, id + "F30", { "sketchPlane" : qUnion([Q0])});
            skPoint(sketch, "E128.0", {"position": v(53.02, 25) * mm});
            skLineSegment(sketch, "E129.bottom", {"start": v(53.02, 25) * mm, "end": v(96.02, 25) * mm});
            skLineSegment(sketch, "E129.top", {"start": v(53.02, 65) * mm, "end": v(96.02, 65) * mm});
            skLineSegment(sketch, "E129.left", {"start": v(53.02, 25) * mm, "end": v(53.02, 65) * mm});
            skLineSegment(sketch, "E129.right", {"start": v(96.02, 25) * mm, "end": v(96.02, 65) * mm});
            skSolve(sketch);
        }
        {
            var Q0;
            Q0 = qSketchRegion(id + "F30", true);
            extrude(context, id + "F31", {"entities" : qUnion([Q0]), "depth" : 43 * mm});
        }
        {
            var Q0;
            Q0=makeQuery(id+"F31.opExtrude","SWEPT_FACE",FACE,{"disambiguationData":[OSD([sQuery(id+"F30.wireOp",EDGE,"E129.top")])]});
            var sketch = newSketch(context, id + "F32", { "sketchPlane" : qUnion([Q0])});
            skSolve(sketch);
        }
        {
            var Q0;
            {var subQ0=sQuery(id+"F30.wireOp",EDGE,"E129.top");Q0=makeQuery(id+"F32.imprint","IMPRINT",FACE,{"disambiguationData":[TD([[makeQuery(id+"F32.imprint","IMPRINT",EDGE,{"derivedFrom":makeQuery(id+"F31.opExtrude","CAP_EDGE",EDGE,{"disambiguationData":[OSD([subQ0])],"isStart":true})}),-1.0]])]});}
            var sketch = newSketch(context, id + "F33", { "sketchPlane" : qUnion([Q0])});
            skLineSegment(sketch, "E130.0", {"start": v(53.02, -43) * mm, "end": v(96.02, -43) * mm, "construction": true});
            skLineSegment(sketch, "E131.0", {"start": v(96.02, -43) * mm, "end": v(96.02, 0) * mm, "construction": true});
            skCircle(sketch, "E132", {"center": v(74.52, -21.5) * mm, "radius": 2.5 * mm});
            skPoint(sketch, "E132.centerSnap0", {"position": v(96.02, -21.5) * mm});
            skPoint(sketch, "E132.centerSnap1", {"position": v(74.52, -43) * mm});
            skSolve(sketch);
        }
        {
            var Q0;
            Q0 = qSketchRegion(id + "F33", true);
            extrude(context, id + "F34", {"entities" : qUnion([Q0]), "operationType" : NewBodyOperationType.ADD, "depth" : 25 * mm});
        }
        {
            var Q0;
            Q0=makeQuery(id+"F28.opExtrude","CAP_FACE",FACE,{"disambiguationData":[OSD([sQuery(id+"F27.wireOp",EDGE,"E68.0"),sQuery(id+"F27.wireOp",EDGE,"E69.0"),sQuery(id+"F27.wireOp",EDGE,"E70.0"),sQuery(id+"F27.wireOp",EDGE,"E71.0"),sQuery(id+"F27.wireOp",EDGE,"E81"),sQuery(id+"F27.wireOp",EDGE,"E82.MirrorC"),sQuery(id+"F27.wireOp",EDGE,"E83.MirrorC"),sQuery(id+"F27.wireOp",EDGE,"E84.MirrorC"),sQuery(id+"F27.wireOp",EDGE,"E85"),sQuery(id+"F27.wireOp",EDGE,"E86.MirrorC"),sQuery(id+"F27.wireOp",EDGE,"E91.MirrorC"),sQuery(id+"F27.wireOp",EDGE,"E92.MirrorC"),sQuery(id+"F27.wireOp",EDGE,"E96.MirrorC"),sQuery(id+"F27.wireOp",EDGE,"E97.MirrorC"),sQuery(id+"F27.wireOp",EDGE,"E99.bottom"),sQuery(id+"F27.wireOp",EDGE,"E99.top"),sQuery(id+"F27.wireOp",EDGE,"E99.left"),sQuery(id+"F27.wireOp",EDGE,"E99.right"),sQuery(id+"F27.wireOp",EDGE,"E100"),sQuery(id+"F27.wireOp",EDGE,"E101"),sQuery(id+"F27.wireOp",EDGE,"E102"),sQuery(id+"F27.wireOp",EDGE,"w5tkOSiS-79zT-Ix9b-OphN-eBkAL5gpQ24t"),sQuery(id+"F27.wireOp",EDGE,"E103"),sQuery(id+"F27.wireOp",EDGE,"TEMbkpEK-8kXP-iDgy-SPFr-wUDxhQlcmG9e"),sQuery(id+"F27.wireOp",EDGE,"E104"),sQuery(id+"F27.wireOp",EDGE,"E105"),sQuery(id+"F27.wireOp",EDGE,"E106"),sQuery(id+"F27.wireOp",EDGE,"E107")])],"isStart":false});
            var sketch = newSketch(context, id + "F35", { "sketchPlane" : qUnion([Q0])});
            skLineSegment(sketch, "E133.bottom", {"start": v(87.3, 144.7) * mm, "end": v(257.3, 144.7) * mm});
            skLineSegment(sketch, "E133.top", {"start": v(87.3, 124.7) * mm, "end": v(257.3, 124.7) * mm});
            skLineSegment(sketch, "E133.left", {"start": v(87.3, 144.7) * mm, "end": v(87.3, 124.7) * mm});
            skLineSegment(sketch, "E133.right", {"start": v(257.3, 144.7) * mm, "end": v(257.3, 124.7) * mm});
            skSolve(sketch);
        }
        {
            var Q0;
            Q0 = qSketchRegion(id + "F35", true);
            extrude(context, id + "F36", {"entities" : qUnion([Q0]), "depth" : 20 * mm});
        }
        {
            var Q0;
            Q0=makeQuery(id+"F28.opExtrude","SWEPT_EDGE",EDGE,{"disambiguationData":[OSD([sQuery(id+"F27.wireOp",EDGE,"E125"),sQuery(id+"F27.wireOp",EDGE,"E126")])]});
            fillet(context, id + "F37", {"entities" : qUnion([Q0]), "radius" : 3 * mm, "tangentPropagation" : true, "allowEdgeOverflow" : false});
        }
        {
            var Q0;
            Q0=makeQuery(id+"F34.opExtrude","CAP_FACE",FACE,{"disambiguationData":[OSD([sQuery(id+"F33.wireOp",EDGE,"E132")])],"isStart":false});
            extrude(context, id + "F38", {"entities" : qUnion([Q0]), "depth" : 200 * mm});
        }
        {
            var Q0;
            Q0=makeQuery(id+"F28.opExtrude","CAP_FACE",FACE,{"disambiguationData":[OSD([sQuery(id+"F27.wireOp",EDGE,"E68.0"),sQuery(id+"F27.wireOp",EDGE,"E69.0"),sQuery(id+"F27.wireOp",EDGE,"E70.0"),sQuery(id+"F27.wireOp",EDGE,"E71.0"),sQuery(id+"F27.wireOp",EDGE,"E81"),sQuery(id+"F27.wireOp",EDGE,"E82.MirrorC"),sQuery(id+"F27.wireOp",EDGE,"E83.MirrorC"),sQuery(id+"F27.wireOp",EDGE,"E84.MirrorC"),sQuery(id+"F27.wireOp",EDGE,"E85"),sQuery(id+"F27.wireOp",EDGE,"E86.MirrorC"),sQuery(id+"F27.wireOp",EDGE,"E91.MirrorC"),sQuery(id+"F27.wireOp",EDGE,"E92.MirrorC"),sQuery(id+"F27.wireOp",EDGE,"E96.MirrorC"),sQuery(id+"F27.wireOp",EDGE,"E97.MirrorC"),sQuery(id+"F27.wireOp",EDGE,"E99.bottom"),sQuery(id+"F27.wireOp",EDGE,"E99.top"),sQuery(id+"F27.wireOp",EDGE,"E99.left"),sQuery(id+"F27.wireOp",EDGE,"E99.right"),sQuery(id+"F27.wireOp",EDGE,"E100"),sQuery(id+"F27.wireOp",EDGE,"E101"),sQuery(id+"F27.wireOp",EDGE,"E102"),sQuery(id+"F27.wireOp",EDGE,"E103"),sQuery(id+"F27.wireOp",EDGE,"E104"),sQuery(id+"F27.wireOp",EDGE,"E105"),sQuery(id+"F27.wireOp",EDGE,"E106"),sQuery(id+"F27.wireOp",EDGE,"E107"),sQuery(id+"F27.wireOp",EDGE,"E122"),sQuery(id+"F27.wireOp",EDGE,"E123"),sQuery(id+"F27.wireOp",EDGE,"E124"),sQuery(id+"F27.wireOp",EDGE,"E125"),sQuery(id+"F27.wireOp",EDGE,"E126")])],"isStart":false});
            var sketch = newSketch(context, id + "F39", { "sketchPlane" : qUnion([Q0])});
            skLineSegment(sketch, "E134.bottom", {"start": v(86.77, 114.51) * mm, "end": v(59.97, 114.51) * mm});
            skLineSegment(sketch, "E134.top", {"start": v(86.77, 133.96) * mm, "end": v(79.61, 133.96) * mm});
            skLineSegment(sketch, "E134.left", {"start": v(86.77, 114.51) * mm, "end": v(86.77, 133.96) * mm});
            skLineSegment(sketch, "E134.right", {"start": v(59.97, 114.51) * mm, "end": v(59.97, 124.23) * mm});
            skCircle(sketch, "E135.0", {"center": v(81.96, 127.9) * mm, "radius": 1.5 * mm});
            skCircle(sketch, "E136.0", {"center": v(81.96, 117.89) * mm, "radius": 1.5 * mm});
            skLineSegment(sketch, "E137", {"start": v(59.97, 124.23) * mm, "end": v(79.61, 133.96) * mm});
            skPoint(sketch, "E138.orphan", {"position": v(59.97, 133.96) * mm});
            skCircle(sketch, "E139", {"center": v(64.61, 117.89) * mm, "radius": 1.5 * mm});
            skSolve(sketch);
        }
        {
            var Q0;
            Q0 = qSketchRegion(id + "F39", true);
            extrude(context, id + "F40", {"entities" : qUnion([Q0]), "depth" : 15 * mm});
        }
        {
            var Q0;
            Q0=makeQuery(id+"F40.opExtrude","SWEPT_FACE",FACE,{"disambiguationData":[OSD([sQuery(id+"F39.wireOp",EDGE,"E134.bottom")])]});
            var sketch = newSketch(context, id + "F41", { "sketchPlane" : qUnion([Q0])});
            skCircle(sketch, "E140.0", {"center": v(74.52, 21.5) * mm, "radius": 2.5 * mm, "construction": true});
            skCircle(sketch, "E141.cCircle", {"center": v(74.52, 21.5) * mm, "radius": 4.1 * mm, "construction": true});
            skLineSegment(sketch, "E141.0", {"start": v(76.89, 17.4) * mm, "end": v(72.15, 17.4) * mm});
            skLineSegment(sketch, "E141.1", {"start": v(72.15, 17.4) * mm, "end": v(69.78, 21.5) * mm});
            skLineSegment(sketch, "E141.2", {"start": v(69.78, 21.5) * mm, "end": v(72.15, 25.6) * mm});
            skLineSegment(sketch, "E141.3", {"start": v(72.15, 25.6) * mm, "end": v(76.89, 25.6) * mm});
            skLineSegment(sketch, "E141.4", {"start": v(76.89, 25.6) * mm, "end": v(79.25, 21.5) * mm});
            skLineSegment(sketch, "E141.5", {"start": v(79.25, 21.5) * mm, "end": v(76.89, 17.4) * mm});
            skPoint(sketch, "E141.0.midPoint", {"position": v(74.52, 17.4) * mm});
            skSolve(sketch);
        }
        {
            var Q0;
            Q0 = qSketchRegion(id + "F41", true);
            extrude(context, id + "F42", {"entities" : qUnion([Q0]), "operationType" : NewBodyOperationType.REMOVE, "oppositeDirection" : true, "depth" : 7 * mm});
        }
        {
            var Q0;
            Q0=makeQuery(id+"F42.boolean.opBoolean","COPY",FACE,{"derivedFrom":makeQuery(id+"F42.opExtrude","CAP_FACE",FACE,{"disambiguationData":[OSD([sQuery(id+"F41.wireOp",EDGE,"E141.0"),sQuery(id+"F41.wireOp",EDGE,"E141.1"),sQuery(id+"F41.wireOp",EDGE,"E141.2"),sQuery(id+"F41.wireOp",EDGE,"E141.3"),sQuery(id+"F41.wireOp",EDGE,"E141.4"),sQuery(id+"F41.wireOp",EDGE,"E141.5")])],"isStart":false})});
            var sketch = newSketch(context, id + "F43", { "sketchPlane" : qUnion([Q0])});
            skCircle(sketch, "E142", {"center": v(74.52, 21.5) * mm, "radius": 3 * mm});
            skPoint(sketch, "E142.centerSnap0", {"position": v(74.52, 17.4) * mm});
            skSolve(sketch);
        }
        {
            var Q0;
            Q0 = qSketchRegion(id + "F43", true);
            extrude(context, id + "F44", {"entities" : qUnion([Q0]), "operationType" : NewBodyOperationType.REMOVE, "oppositeDirection" : true, "depth" : 25 * mm});
        }
        {
            var Q0;
            Q0=makeQuery(id+"F44.boolean.opBoolean","INTERSECT",EDGE,{"derivedFrom":[makeQuery(id+"F40.opExtrude","SWEPT_FACE",FACE,{"disambiguationData":[OSD([sQuery(id+"F39.wireOp",EDGE,"E137")])]}),makeQuery(id+"F44.opExtrude","SWEPT_FACE",FACE,{"disambiguationData":[OSD([sQuery(id+"F43.wireOp",EDGE,"E142")])]})]});
            fillet(context, id + "F45", {"entities" : qUnion([Q0]), "radius" : 2 * mm, "tangentPropagation" : true, "allowEdgeOverflow" : false});
        }
        {
            var Q0;
            Q0=makeQuery(id+"F40.opExtrude","CAP_FACE",FACE,{"disambiguationData":[OSD([sQuery(id+"F39.wireOp",EDGE,"E134.bottom"),sQuery(id+"F39.wireOp",EDGE,"E134.top"),sQuery(id+"F39.wireOp",EDGE,"E134.left"),sQuery(id+"F39.wireOp",EDGE,"E134.right"),sQuery(id+"F39.wireOp",EDGE,"E135.0"),sQuery(id+"F39.wireOp",EDGE,"E136.0"),sQuery(id+"F39.wireOp",EDGE,"E137"),sQuery(id+"F39.wireOp",EDGE,"E139")])],"isStart":false});
            var sketch = newSketch(context, id + "F46", { "sketchPlane" : qUnion([Q0])});
            skCircle(sketch, "E143", {"center": v(64.61, 117.89) * mm, "radius": 3 * mm});
            skCircle(sketch, "E144", {"center": v(81.96, 117.89) * mm, "radius": 3 * mm});
            skCircle(sketch, "E145", {"center": v(81.96, 127.9) * mm, "radius": 3 * mm});
            skSolve(sketch);
        }
        {
            var Q0;
            Q0 = qSketchRegion(id + "F46", true);
            extrude(context, id + "F47", {"entities" : qUnion([Q0]), "operationType" : NewBodyOperationType.REMOVE, "oppositeDirection" : true, "depth" : 2 * mm});
        }
        {
            var Q0;
            Q0=makeQuery(id+"F36.opExtrude","CAP_FACE",FACE,{"disambiguationData":[OSD([sQuery(id+"F35.wireOp",EDGE,"E133.bottom"),sQuery(id+"F35.wireOp",EDGE,"E133.top"),sQuery(id+"F35.wireOp",EDGE,"E133.left"),sQuery(id+"F35.wireOp",EDGE,"E133.right")])],"isStart":false});
            var Q1;
            Q1=makeQuery(id+"F36.opExtrude","CAP_FACE",FACE,{"disambiguationData":[OSD([sQuery(id+"F35.wireOp",EDGE,"E133.bottom"),sQuery(id+"F35.wireOp",EDGE,"E133.top"),sQuery(id+"F35.wireOp",EDGE,"E133.left"),sQuery(id+"F35.wireOp",EDGE,"E133.right")])],"isStart":true});
            cPlane(context, id + "F48", {"entities" : qUnion([Q0, Q1]), "cplaneType" : CPlaneType.MID_PLANE, "offset" : 25 * mm, "width" : 150 * mm, "height" : 150 * mm});
        }
        {
            var Q0;
            Q0=makeQuery(id+"F28.opExtrude","SWEPT_BODY",BODY,{"disambiguationData":[OSD([sQuery(id+"F27.wireOp",EDGE,"E109.bottom"),sQuery(id+"F27.wireOp",EDGE,"E109.left"),sQuery(id+"F27.wireOp",EDGE,"E109.right"),sQuery(id+"F27.wireOp",EDGE,"E110"),sQuery(id+"F27.wireOp",EDGE,"E111"),sQuery(id+"F27.wireOp",EDGE,"E112"),sQuery(id+"F27.wireOp",EDGE,"E113"),sQuery(id+"F27.wireOp",EDGE,"E116"),sQuery(id+"F27.wireOp",EDGE,"E117.filletArc"),sQuery(id+"F27.wireOp",EDGE,"E120.top"),sQuery(id+"F27.wireOp",EDGE,"E120.left")])]});
            var Q1;
            Q1=qCreatedBy(id+"F48.planeOp",FACE);
            mirror(context, id + "F49", {"entities" : qUnion([Q0]), "mirrorPlane" : qUnion([Q1])});
        }
        {
            var Q0;
            Q0=makeQuery(id+"F49.opPattern","COPY",FACE,{"derivedFrom":makeQuery(id+"F28.opExtrude","CAP_FACE",FACE,{"disambiguationData":[OSD([sQuery(id+"F27.wireOp",EDGE,"E109.bottom"),sQuery(id+"F27.wireOp",EDGE,"E109.left"),sQuery(id+"F27.wireOp",EDGE,"E109.right"),sQuery(id+"F27.wireOp",EDGE,"E110"),sQuery(id+"F27.wireOp",EDGE,"E111"),sQuery(id+"F27.wireOp",EDGE,"E112"),sQuery(id+"F27.wireOp",EDGE,"E113"),sQuery(id+"F27.wireOp",EDGE,"E116"),sQuery(id+"F27.wireOp",EDGE,"E117.filletArc"),sQuery(id+"F27.wireOp",EDGE,"E120.top"),sQuery(id+"F27.wireOp",EDGE,"E120.left")])],"isStart":true}),"instanceName":"1"});
            extrude(context, id + "F50", {"entities" : qUnion([Q0]), "operationType" : NewBodyOperationType.REMOVE, "oppositeDirection" : true, "depth" : 5 * mm});
        }
        {
            var Q0;
            Q0=makeQuery(id+"F28.opExtrude","CAP_FACE",FACE,{"disambiguationData":[OSD([sQuery(id+"F27.wireOp",EDGE,"E109.bottom"),sQuery(id+"F27.wireOp",EDGE,"E109.left"),sQuery(id+"F27.wireOp",EDGE,"E109.right"),sQuery(id+"F27.wireOp",EDGE,"E110"),sQuery(id+"F27.wireOp",EDGE,"E111"),sQuery(id+"F27.wireOp",EDGE,"E112"),sQuery(id+"F27.wireOp",EDGE,"E113"),sQuery(id+"F27.wireOp",EDGE,"E116"),sQuery(id+"F27.wireOp",EDGE,"E117.filletArc"),sQuery(id+"F27.wireOp",EDGE,"E120.top"),sQuery(id+"F27.wireOp",EDGE,"E120.left")])],"isStart":true});
            extrude(context, id + "F51", {"entities" : qUnion([Q0]), "operationType" : NewBodyOperationType.REMOVE, "oppositeDirection" : true, "depth" : 5 * mm});
        }
        {
            var Q0;
            Q0=makeQuery(id+"F28.opExtrude","CAP_FACE",FACE,{"disambiguationData":[OSD([sQuery(id+"F27.wireOp",EDGE,"E68.0"),sQuery(id+"F27.wireOp",EDGE,"E69.0"),sQuery(id+"F27.wireOp",EDGE,"E70.0"),sQuery(id+"F27.wireOp",EDGE,"E71.0"),sQuery(id+"F27.wireOp",EDGE,"E81"),sQuery(id+"F27.wireOp",EDGE,"E82.MirrorC"),sQuery(id+"F27.wireOp",EDGE,"E83.MirrorC"),sQuery(id+"F27.wireOp",EDGE,"E84.MirrorC"),sQuery(id+"F27.wireOp",EDGE,"E85"),sQuery(id+"F27.wireOp",EDGE,"E86.MirrorC"),sQuery(id+"F27.wireOp",EDGE,"E91.MirrorC"),sQuery(id+"F27.wireOp",EDGE,"E92.MirrorC"),sQuery(id+"F27.wireOp",EDGE,"E96.MirrorC"),sQuery(id+"F27.wireOp",EDGE,"E97.MirrorC"),sQuery(id+"F27.wireOp",EDGE,"E99.bottom"),sQuery(id+"F27.wireOp",EDGE,"E99.top"),sQuery(id+"F27.wireOp",EDGE,"E99.left"),sQuery(id+"F27.wireOp",EDGE,"E99.right"),sQuery(id+"F27.wireOp",EDGE,"E100"),sQuery(id+"F27.wireOp",EDGE,"E101"),sQuery(id+"F27.wireOp",EDGE,"E102"),sQuery(id+"F27.wireOp",EDGE,"E103"),sQuery(id+"F27.wireOp",EDGE,"E104"),sQuery(id+"F27.wireOp",EDGE,"E105"),sQuery(id+"F27.wireOp",EDGE,"E106"),sQuery(id+"F27.wireOp",EDGE,"E107"),sQuery(id+"F27.wireOp",EDGE,"E122"),sQuery(id+"F27.wireOp",EDGE,"E123"),sQuery(id+"F27.wireOp",EDGE,"E124"),sQuery(id+"F27.wireOp",EDGE,"E125"),sQuery(id+"F27.wireOp",EDGE,"E126")])],"isStart":true});
            var sketch = newSketch(context, id + "F52", { "sketchPlane" : qUnion([Q0])});
            skLineSegment(sketch, "E146.bottom", {"start": v(-8.28, 167.06) * mm, "end": v(-50.58, 167.06) * mm});
            skLineSegment(sketch, "E146.top", {"start": v(-8.28, 124.76) * mm, "end": v(-50.58, 124.76) * mm});
            skLineSegment(sketch, "E146.left", {"start": v(-8.28, 167.06) * mm, "end": v(-8.28, 124.76) * mm});
            skLineSegment(sketch, "E146.right", {"start": v(-50.58, 167.06) * mm, "end": v(-50.58, 124.76) * mm});
            skPoint(sketch, "E146.middle", {"position": v(-29.43, 145.9) * mm});
            skLineSegment(sketch, "E147.bottom", {"start": v(-8.28, 78.64) * mm, "end": v(-50.58, 78.64) * mm});
            skLineSegment(sketch, "E147.top", {"start": v(-8.28, 120.94) * mm, "end": v(-50.58, 120.94) * mm});
            skLineSegment(sketch, "E147.left", {"start": v(-8.28, 78.64) * mm, "end": v(-8.28, 120.94) * mm});
            skLineSegment(sketch, "E147.right", {"start": v(-50.58, 78.64) * mm, "end": v(-50.58, 120.94) * mm});
            skPoint(sketch, "E147.middle", {"position": v(-29.43, 99.8) * mm});
            skSolve(sketch);
        }
        {
            var Q0;
            Q0 = qSketchRegion(id + "F52", true);
            extrude(context, id + "F53", {"entities" : qUnion([Q0]), "depth" : 40 * mm});
        }
        {
            var Q0;
            Q0=makeQuery(id+"F15.opExtrude","CAP_FACE",FACE,{"disambiguationData":[OSD([sQuery(id+"F14.wireOp",EDGE,"E37.bottom"),sQuery(id+"F14.wireOp",EDGE,"E37.top"),sQuery(id+"F14.wireOp",EDGE,"E37.left"),sQuery(id+"F14.wireOp",EDGE,"E37.right")])],"isStart":false});
            var sketch = newSketch(context, id + "F54", { "sketchPlane" : qUnion([Q0])});
            skLineSegment(sketch, "E148.bottom", {"start": v(103.02, 99) * mm, "end": v(223.02, 99) * mm});
            skLineSegment(sketch, "E148.top", {"start": v(103.02, -71) * mm, "end": v(223.02, -71) * mm});
            skLineSegment(sketch, "E148.left", {"start": v(103.02, 99) * mm, "end": v(103.02, -71) * mm});
            skLineSegment(sketch, "E148.right", {"start": v(223.02, 99) * mm, "end": v(223.02, -71) * mm});
            skPoint(sketch, "E148.middle", {"position": v(163.02, 14) * mm});
            skPoint(sketch, "E148.middle.positionSnap0", {"position": v(163.02, 34) * mm});
            skPoint(sketch, "E148.middle.positionSnap1", {"position": v(173.02, 14) * mm});
            skPoint(sketch, "E148.centerSnap0", {"position": v(163.02, 34) * mm});
            skPoint(sketch, "E148.centerSnap1", {"position": v(173.02, 14) * mm});
            skSolve(sketch);
        }
        {
            var Q0;
            Q0 = qSketchRegion(id + "F54", true);
            extrude(context, id + "F55", {"entities" : qUnion([Q0]), "depth" : 18 * mm});
        }
        {
            var Q0;
            Q0=makeQuery(id+"F36.opExtrude","SWEPT_FACE",FACE,{"disambiguationData":[OSD([sQuery(id+"F35.wireOp",EDGE,"E133.bottom")])]});
            var sketch = newSketch(context, id + "F56", { "sketchPlane" : qUnion([Q0])});
            skLineSegment(sketch, "E149.bottom", {"start": v(92.13, -21.3) * mm, "end": v(242.13, -21.3) * mm});
            skLineSegment(sketch, "E149.top", {"start": v(92.13, -30.3) * mm, "end": v(242.13, -30.3) * mm});
            skLineSegment(sketch, "E149.left", {"start": v(92.13, -21.3) * mm, "end": v(92.13, -30.3) * mm});
            skLineSegment(sketch, "E149.right", {"start": v(242.13, -21.3) * mm, "end": v(242.13, -30.3) * mm});
            skPoint(sketch, "E149.middle", {"position": v(167.13, -25.8) * mm});
            skPoint(sketch, "E149.middle.positionSnap0", {"position": v(257.3, -25.8) * mm});
            skPoint(sketch, "E149.centerSnap0", {"position": v(257.3, -25.8) * mm});
            skSolve(sketch);
        }
        {
            var Q0;
            Q0 = qSketchRegion(id + "F56", true);
            extrude(context, id + "F57", {"entities" : qUnion([Q0]), "depth" : 6 * mm});
        }
        {
            var Q0;
            Q0=makeQuery(id+"F57.opExtrude","CAP_FACE",FACE,{"disambiguationData":[OSD([sQuery(id+"F56.wireOp",EDGE,"E149.bottom"),sQuery(id+"F56.wireOp",EDGE,"E149.top"),sQuery(id+"F56.wireOp",EDGE,"E149.left"),sQuery(id+"F56.wireOp",EDGE,"E149.right")])],"isStart":false});
            var sketch = newSketch(context, id + "F58", { "sketchPlane" : qUnion([Q0])});
            skLineSegment(sketch, "E150.bottom", {"start": v(182.13, -15.8) * mm, "end": v(152.13, -15.8) * mm});
            skLineSegment(sketch, "E150.top", {"start": v(182.13, -35.8) * mm, "end": v(152.13, -35.8) * mm});
            skLineSegment(sketch, "E150.left", {"start": v(182.13, -15.8) * mm, "end": v(182.13, -35.8) * mm});
            skLineSegment(sketch, "E150.right", {"start": v(152.13, -15.8) * mm, "end": v(152.13, -35.8) * mm});
            skPoint(sketch, "E150.middle", {"position": v(167.13, -25.8) * mm});
            skPoint(sketch, "E150.middle.positionSnap0", {"position": v(167.13, -21.3) * mm});
            skPoint(sketch, "E150.middle.positionSnap1", {"position": v(92.13, -25.8) * mm});
            skPoint(sketch, "E150.centerSnap0", {"position": v(167.13, -21.3) * mm});
            skPoint(sketch, "E150.centerSnap1", {"position": v(92.13, -25.8) * mm});
            skSolve(sketch);
        }
        {
            var Q0;
            Q0 = qSketchRegion(id + "F58", true);
            extrude(context, id + "F59", {"entities" : qUnion([Q0]), "endBound" : BoundingType.SYMMETRIC, "depth" : 6 * mm});
        }
        {
            var Q0;
            Q0=makeQuery(id+"F49.opPattern","COPY",BODY,{"derivedFrom":makeQuery(id+"F28.opExtrude","SWEPT_BODY",BODY,{"disambiguationData":[OSD([sQuery(id+"F27.wireOp",EDGE,"E109.bottom"),sQuery(id+"F27.wireOp",EDGE,"E109.left"),sQuery(id+"F27.wireOp",EDGE,"E109.right"),sQuery(id+"F27.wireOp",EDGE,"E110"),sQuery(id+"F27.wireOp",EDGE,"E111"),sQuery(id+"F27.wireOp",EDGE,"E112"),sQuery(id+"F27.wireOp",EDGE,"E113"),sQuery(id+"F27.wireOp",EDGE,"E116"),sQuery(id+"F27.wireOp",EDGE,"E117.filletArc"),sQuery(id+"F27.wireOp",EDGE,"E120.top"),sQuery(id+"F27.wireOp",EDGE,"E120.left")])]}),"instanceName":"1"});
            var Q1;
            Q1=makeQuery(id+"F28.opExtrude","SWEPT_BODY",BODY,{"disambiguationData":[OSD([sQuery(id+"F27.wireOp",EDGE,"E109.bottom"),sQuery(id+"F27.wireOp",EDGE,"E109.left"),sQuery(id+"F27.wireOp",EDGE,"E109.right"),sQuery(id+"F27.wireOp",EDGE,"E110"),sQuery(id+"F27.wireOp",EDGE,"E111"),sQuery(id+"F27.wireOp",EDGE,"E112"),sQuery(id+"F27.wireOp",EDGE,"E113"),sQuery(id+"F27.wireOp",EDGE,"E116"),sQuery(id+"F27.wireOp",EDGE,"E117.filletArc"),sQuery(id+"F27.wireOp",EDGE,"E120.top"),sQuery(id+"F27.wireOp",EDGE,"E120.left")])]});
            transform(context, id + "F60", {"entities" : qUnion([Q0, Q1]), "transformType" : TransformType.TRANSLATION_3D, "dx" : -22.7 * mm, "dy" : 0 * mm, "dz" : 0 * mm, "makeCopy" : false});
        }
        {
            var Q0;
            Q0=makeQuery(id+"F59.opExtrude","CAP_FACE",FACE,{"disambiguationData":[OSD([sQuery(id+"F58.wireOp",EDGE,"E150.bottom"),sQuery(id+"F58.wireOp",EDGE,"E150.top"),sQuery(id+"F58.wireOp",EDGE,"E150.left"),sQuery(id+"F58.wireOp",EDGE,"E150.right")])],"isStart":false});
            var sketch = newSketch(context, id + "F61", { "sketchPlane" : qUnion([Q0])});
            skLineSegment(sketch, "E151.bottom", {"start": v(152.13, -15.8) * mm, "end": v(182.13, -15.8) * mm});
            skLineSegment(sketch, "E151.top", {"start": v(152.13, -68.1) * mm, "end": v(161.13, -68.1) * mm});
            skLineSegment(sketch, "E151.left", {"start": v(152.13, -15.8) * mm, "end": v(152.13, -68.1) * mm});
            skLineSegment(sketch, "E151.right", {"start": v(182.13, -15.8) * mm, "end": v(182.13, -68.1) * mm});
            skLineSegment(sketch, "E152.left", {"start": v(173.13, -58.14) * mm, "end": v(173.13, -68.1) * mm});
            skLineSegment(sketch, "E152.right", {"start": v(161.13, -58.14) * mm, "end": v(161.13, -68.1) * mm});
            skPoint(sketch, "E152.middle", {"position": v(167.13, -68.1) * mm});
            skArc(sketch, "E153", {"start": v(173.13, -58.14) * mm, "mid": v(167.13, -52.14) * mm, "end": v(161.13, -58.14) * mm});
            skPoint(sketch, "E153.centerSnap0", {"position": v(167.13, -53.1) * mm});
            skPoint(sketch, "E154.orphan", {"position": v(161.13, -53.1) * mm});
            skPoint(sketch, "E155.orphan", {"position": v(173.13, -53.1) * mm});
            skLineSegment(sketch, "E156.trimOffspring", {"start": v(173.13, -68.1) * mm, "end": v(182.13, -68.1) * mm});
            skPoint(sketch, "E152.top.end.orphan", {"position": v(161.13, -83.1) * mm});
            skPoint(sketch, "E152.top.start.orphan", {"position": v(173.13, -83.1) * mm});
            skLineSegment(sketch, "E157.bottom", {"start": v(174.13, -19.3) * mm, "end": v(160.13, -19.3) * mm, "construction": true});
            skLineSegment(sketch, "E157.top", {"start": v(174.13, -32.3) * mm, "end": v(160.13, -32.3) * mm, "construction": true});
            skLineSegment(sketch, "E157.left", {"start": v(174.13, -19.3) * mm, "end": v(174.13, -32.3) * mm, "construction": true});
            skLineSegment(sketch, "E157.right", {"start": v(160.13, -19.3) * mm, "end": v(160.13, -32.3) * mm, "construction": true});
            skPoint(sketch, "E157.middle", {"position": v(167.13, -25.8) * mm});
            skPoint(sketch, "E157.middle.positionSnap0", {"position": v(152.13, -25.8) * mm});
            skPoint(sketch, "E157.middle.positionSnap1", {"position": v(167.13, -15.8) * mm});
            skPoint(sketch, "E157.centerSnap0", {"position": v(152.13, -25.8) * mm});
            skPoint(sketch, "E157.centerSnap1", {"position": v(167.13, -15.8) * mm});
            skCircle(sketch, "E158", {"center": v(174.13, -19.3) * mm, "radius": 1.5 * mm});
            skCircle(sketch, "E159", {"center": v(160.13, -19.3) * mm, "radius": 1.5 * mm});
            skCircle(sketch, "E160", {"center": v(160.13, -32.3) * mm, "radius": 1.5 * mm});
            skCircle(sketch, "E161", {"center": v(174.13, -32.3) * mm, "radius": 1.5 * mm});
            skCircle(sketch, "E162", {"center": v(179.21, -58.14) * mm, "radius": 1.5 * mm});
            skLineSegment(sketch, "E163", {"start": v(167.13, -68.1) * mm, "end": v(167.13, -3.43) * mm, "construction": true});
            skCircle(sketch, "E164.MirrorC", {"center": v(155.05, -58.14) * mm, "radius": 1.5 * mm});
            skLineSegment(sketch, "E165.bottom", {"start": v(155.73, -37.81) * mm, "end": v(157.73, -37.81) * mm});
            skLineSegment(sketch, "E165.top", {"start": v(155.73, -49.81) * mm, "end": v(157.73, -49.81) * mm});
            skLineSegment(sketch, "E165.left", {"start": v(155.73, -37.81) * mm, "end": v(155.73, -49.81) * mm});
            skLineSegment(sketch, "E165.right", {"start": v(157.73, -37.81) * mm, "end": v(157.73, -49.81) * mm});
            skCircle(sketch, "E166", {"center": v(167.13, -39.12) * mm, "radius": 1.5 * mm});
            skLineSegment(sketch, "E167.MirrorCS", {"start": v(178.53, -49.81) * mm, "end": v(176.53, -49.81) * mm});
            skLineSegment(sketch, "E168.MirrorCS", {"start": v(178.53, -37.81) * mm, "end": v(176.53, -37.81) * mm});
            skLineSegment(sketch, "E169.MirrorCS", {"start": v(176.53, -37.81) * mm, "end": v(176.53, -49.81) * mm});
            skLineSegment(sketch, "E170.MirrorCS", {"start": v(178.53, -37.81) * mm, "end": v(178.53, -49.81) * mm});
            skSolve(sketch);
        }
        {
            var Q0;
            Q0 = qSketchRegion(id + "F61", true);
            extrude(context, id + "F62", {"entities" : qUnion([Q0]), "depth" : 5 * mm});
        }
    });
